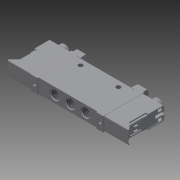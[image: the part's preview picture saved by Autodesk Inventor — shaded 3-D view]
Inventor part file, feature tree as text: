
AUTODESK INVENTOR PART (.ipt)
format: ipt  version: 2014 SP2 (Build 180246200, 246)  size: 827,904 bytes
history: native  units: mm
features: other x112, sketch x70, extrude x53, revolve x13, hole x4, thread x3
ambient origin geometry x8: Origin, YZ Plane, XZ Plane, XY Plane, X Axis, Y Axis, Z Axis, Center Point
bodies: Solid1 (feature_tree)
feature tree (255):
  extrude  "Extrusion1"  Depth=12.0mm TaperAngle=0.0deg
  extrude  "Extrusion2"  TaperAngle=360.0deg  [1 undecoded]
  extrude  "Extrusion3"  TaperAngle=360.0deg  [1 undecoded]
  sketch  "Sketch_5"  dims[d4=12.0mm d5=0.0mm d6=360.0deg]
  sketch  "Sketch_6"  dims[d7=5.4585mm d8=0.0mm d9=360.0deg]
  sketch  "Sketch_7"  dims[d10=5.4585mm d11=0.0mm d12=360.0deg d13=5.4585mm d14=0.0mm]
  revolve  "Revolution1"  Angle=360.0deg
  thread  "Thread1"  [1 undecoded]
  revolve  "Revolution2"  [1 undecoded]
  thread  "Thread2"  [1 undecoded]
  revolve  "Revolution3"  [1 undecoded]
  thread  "Thread3"  [1 undecoded]
  hole  "Hole1"  [1 undecoded]
  hole  "Hole2"  [1 undecoded]
  hole  "Hole3"  [1 undecoded]
  hole  "Hole4"  [1 undecoded]
  extrude  "Extrusion4"  Depth=5.7mm TaperAngle=0.0deg
  extrude  "Extrusion5"  Depth=4.0mm TaperAngle=0.0deg
  sketch  "Sketch_19"  dims[d57=3.1mm d58=0.0mm d59=0.1mm d60=0.0mm]
  extrude  "Extrusion6"  Depth=5.0mm TaperAngle=0.0deg
  extrude  "Extrusion7"  Depth=12.0mm TaperAngle=0.0deg
  extrude  "Extrusion8"  Depth=3.1mm TaperAngle=0.0deg
  extrude  "Extrusion9"  Depth=1.0mm TaperAngle=0.0deg
  extrude  "Extrusion10"  TaperAngle=360.0deg  [1 undecoded]
  extrude  "Extrusion11"  TaperAngle=360.0deg  [1 undecoded]
  extrude  "Extrusion12"  Depth=3.0mm TaperAngle=0.0deg
  extrude  "Extrusion13"  TaperAngle=360.0deg  [1 undecoded]
  extrude  "Extrusion14"  TaperAngle=360.0deg  [1 undecoded]
  revolve  "Revolution4"  Angle=360.0deg
  extrude  "Extrusion15"  Depth=2.15mm TaperAngle=0.0deg
  extrude  "Extrusion16"  Depth=7.8mm TaperAngle=0.0deg
  extrude  "Extrusion17"  Depth=2.1mm TaperAngle=0.0deg
  extrude  "Extrusion18"  Depth=7.8mm TaperAngle=0.0deg
  extrude  "Extrusion19"  Depth=2.8mm TaperAngle=0.0deg
  extrude  "Extrusion20"  Depth=1.5mm TaperAngle=0.0deg
  extrude  "Extrusion21"  Depth=3.0mm TaperAngle=0.0deg
  extrude  "Extrusion22"  Depth=3.0mm TaperAngle=0.0deg
  extrude  "Extrusion23"  Depth=2.0mm TaperAngle=0.0deg
  extrude  "Extrusion24"  Depth=2.0mm TaperAngle=0.0deg
  extrude  "Extrusion25"  Depth=2.0mm TaperAngle=0.0deg
  extrude  "Extrusion26"  [1 undecoded]
  extrude  "Extrusion27"  [1 undecoded]
  extrude  "Extrusion28"  [1 undecoded]
  revolve  "Revolution5"  [1 undecoded]
  revolve  "Revolution6"  [1 undecoded]
  revolve  "Revolution7"  [1 undecoded]
  sketch  "Sketch_59"
  sketch  "Sketch_56"
  extrude  "Extrusion29"  [1 undecoded]
  extrude  "Extrusion30"  [1 undecoded]
  revolve  "Revolution8"  [1 undecoded]
  revolve  "Revolution9"  [1 undecoded]
  revolve  "Revolution10"  [1 undecoded]
  revolve  "Revolution11"  [1 undecoded]
  revolve  "Revolution12"  [1 undecoded]
  revolve  "Revolution13"  [1 undecoded]
  extrude  "Extrusion31"  [1 undecoded]
  extrude  "Extrusion32"  [1 undecoded]
  extrude  "Extrusion33"  [1 undecoded]
  extrude  "Extrusion34"  [1 undecoded]
  extrude  "Extrusion35"  [1 undecoded]
  extrude  "Extrusion36"  [1 undecoded]
  extrude  "Extrusion37"  [1 undecoded]
  extrude  "Extrusion38"  [1 undecoded]
  extrude  "Extrusion39"  [1 undecoded]
  extrude  "Extrusion40"  [1 undecoded]
  extrude  "Extrusion41"  [1 undecoded]
  extrude  "Extrusion42"  [1 undecoded]
  extrude  "Extrusion43"  [1 undecoded]
  extrude  "Extrusion44"  [1 undecoded]
  extrude  "Extrusion45"  [1 undecoded]
  extrude  "Extrusion46"  [1 undecoded]
  extrude  "Extrusion47"  [1 undecoded]
  extrude  "Extrusion48"  [1 undecoded]
  extrude  "Extrusion49"  [1 undecoded]
  extrude  "Extrusion50"  [1 undecoded]
  extrude  "Extrusion51"  [1 undecoded]
  extrude  "Extrusion52"  [1 undecoded]
  extrude  "Extrusion53"  [1 undecoded]
  other  "DICHTUNG_XY"
  other  "DICHTUNG_YZ"
  other  "DICHTUNG_ZX"
  other  "DICHTUNG_X"
  other  "DICHTUNG_Y"
  other  "DICHTUNG_Z"
  other  "DICHTUNG_Center"
  other  "GEHAUSE_XY"
  other  "GEHAUSE_YZ"
  other  "GEHAUSE_ZX"
  other  "GEHAUSE_X"
  other  "GEHAUSE_Y"
  other  "GEHAUSE_Z"
  other  "GEHAUSE_Center"
  other  "HHB1_XY"
  other  "HHB1_YZ"
  other  "HHB1_ZX"
  other  "HHB1_X"
  other  "HHB1_Y"
  other  "HHB1_Z"
  other  "HHB1_Center"
  other  "HHB2_XY"
  other  "HHB2_YZ"
  other  "HHB2_ZX"
  other  "HHB2_X"
  other  "HHB2_Y"
  other  "HHB2_Z"
  other  "HHB2_Center"
  other  "NEBV1_XY"
  other  "NEBV1_YZ"
  other  "NEBV1_ZX"
  other  "NEBV1_X"
  other  "NEBV1_Y"
  other  "NEBV1_Z"
  other  "NEBV1_Center"
  other  "NEBV2_XY"
  other  "NEBV2_YZ"
  other  "NEBV2_ZX"
  other  "NEBV2_X"
  other  "NEBV2_Y"
  other  "NEBV2_Z"
  other  "NEBV2_Center"
  other  "QS_K1_XY"
  other  "QS_K1_YZ"
  other  "QS_K1_ZX"
  other  "QS_K1_X"
  other  "QS_K1_Y"
  other  "QS_K1_Z"
  other  "QS_K1_Center"
  other  "QS_K1214_XY"
  other  "QS_K1214_YZ"
  other  "QS_K1214_ZX"
  other  "QS_K1214_X"
  other  "QS_K1214_Y"
  other  "QS_K1214_Z"
  other  "QS_K1214_Center"
  other  "QS_K2_XY"
  other  "QS_K2_YZ"
  other  "QS_K2_ZX"
  other  "QS_K2_X"
  other  "QS_K2_Y"
  other  "QS_K2_Z"
  other  "QS_K2_Center"
  other  "QS_K3_XY"
  other  "QS_K3_YZ"
  other  "QS_K3_ZX"
  other  "QS_K3_X"
  other  "QS_K3_Y"
  other  "QS_K3_Z"
  other  "QS_K3_Center"
  other  "QS_K4_XY"
  other  "QS_K4_YZ"
  other  "QS_K4_ZX"
  other  "QS_K4_X"
  other  "QS_K4_Y"
  other  "QS_K4_Z"
  other  "QS_K4_Center"
  other  "QS_K5_XY"
  other  "QS_K5_YZ"
  other  "QS_K5_ZX"
  other  "QS_K5_X"
  other  "QS_K5_Y"
  other  "QS_K5_Z"
  other  "QS_K5_Center"
  other  "SCREW1_XY"
  other  "SCREW1_YZ"
  other  "SCREW1_ZX"
  other  "SCREW1_X"
  other  "SCREW1_Y"
  other  "SCREW1_Z"
  other  "SCREW1_Center"
  other  "SCREW2_XY"
  other  "SCREW2_YZ"
  other  "SCREW2_ZX"
  other  "SCREW2_X"
  other  "SCREW2_Y"
  other  "SCREW2_Z"
  other  "SCREW2_Center"
  other  "VAVE1_XY"
  other  "VAVE1_YZ"
  other  "VAVE1_ZX"
  other  "VAVE1_X"
  other  "VAVE1_Y"
  other  "VAVE1_Z"
  other  "VAVE1_Center"
  other  "VAVE2_XY"
  other  "VAVE2_YZ"
  other  "VAVE2_ZX"
  other  "VAVE2_X"
  other  "VAVE2_Y"
  other  "VAVE2_Z"
  other  "VAVE2_Center"
  sketch  "Sketch_53"  dims[d147=2.0mm d148=0.0mm d149=2.0mm d150=0.0mm]
  sketch  "Sketch_54"  dims[d151=2.0mm d152=0.0mm]
  sketch  "Sketch_55"  dims[d153=0.0mm d154=0.0mm d155=0.0mm d156=0.0mm d157=0.0mm d158=0.0mm d159=0.0mm d160=0.0mm d161=0.0mm d162=0.0mm]
  sketch  "Sketch7"  dims[d15=5.917468mm d16=6.5415mm d17=7.0mm d18=2.0mm d19=90.0deg d20=6.8mm d21=0.0mm]
  sketch  "Sketch8"  dims[d22=5.917468mm d23=6.5415mm d24=7.0mm d25=2.0mm d26=90.0deg d27=6.8mm d28=0.0mm]
  sketch  "Sketch9"  dims[d29=3.0mm d30=6.0mm d31=4.0mm d32=2.0mm d33=90.0deg d34=6.7mm d35=0.0mm]
  sketch  "Sketch10"  dims[d36=3.0mm d37=6.0mm d38=4.0mm d39=2.0mm d40=90.0deg d41=6.7mm d42=0.0mm d43=33.1mm d44=0.0mm d45=5.7mm d46=0.0mm]
  sketch  "Sketch_17"  dims[d53=12.0mm d54=0.0mm d55=12.0mm d56=0.0mm]
  sketch  "Sketch_20"  dims[d61=1.0mm d62=0.0mm d63=2.6mm d64=0.0mm]
  sketch  "Sketch_30"  dims[d97=3.0mm d98=0.0mm d99=3.0mm d100=0.0mm]
  sketch  "Sketch_22"  dims[d68=33.1mm d69=0.0mm d70=5.7mm d71=0.0mm]
  sketch  "Sketch_23"  dims[d72=64.0mm d73=0.0mm d74=4.0mm d75=0.0mm]
  sketch  "Sketch_24"  dims[d76=12.0mm d77=0.0mm d78=5.0mm d79=0.0mm]
  sketch  "Sketch_25"  dims[d80=17.2mm d81=0.0mm d82=12.0mm d83=0.0mm]
  sketch  "Sketch_26"  dims[d84=12.0mm d85=0.0mm d86=3.1mm d87=0.0mm]
  sketch  "Sketch_27"  dims[d88=0.1mm d89=0.0mm d90=1.0mm d91=0.0mm]
  sketch  "Sketch_28"  dims[d92=2.6mm d93=0.0mm d94=360.0deg]
  sketch  "Sketch_29"  dims[d95=360.0deg d96=360.0deg]
  sketch  "Sketch_21"  dims[d65=360.0deg d66=4.0mm d67=0.0mm]
  sketch  "Sketch_31"  dims[d101=360.0deg d102=360.0deg]
  sketch  "Sketch_32"  dims[d103=360.0deg d104=360.0deg]
  sketch  "Sketch_33"  dims[d105=360.0deg d106=360.0deg]
  sketch  "Sketch_119"
  sketch  "Sketch_36"  dims[d111=7.8mm d112=0.0mm d113=7.8mm d114=0.0mm]
  sketch  "Sketch_37"  dims[d115=2.1mm d116=0.0mm d117=2.1mm d118=0.0mm]
  sketch  "Sketch_38"  dims[d119=7.8mm d120=0.0mm d121=7.8mm d122=0.0mm]
  sketch  "Sketch_39"  dims[d123=7.8mm d124=0.0mm d125=2.8mm d126=0.0mm]
  sketch  "Sketch_40"  dims[d127=2.8mm d128=0.0mm d129=1.5mm d130=0.0mm]
  sketch  "Sketch_41"  dims[d131=1.5mm d132=0.0mm d133=3.0mm d134=0.0mm]
  sketch  "Sketch_42"  dims[d135=3.0mm d136=0.0mm d137=3.0mm d138=0.0mm]
  sketch  "Sketch_43"  dims[d139=3.0mm d140=0.0mm d141=2.0mm d142=0.0mm]
  sketch  "Sketch_44"  dims[d143=2.0mm d144=0.0mm d145=2.0mm d146=0.0mm]
  sketch  "Sketch_34"  dims[d107=2.15mm d108=0.0mm d109=2.15mm d110=0.0mm]
  sketch  "Sketch_4"  dims[d0=42.0mm d1=0.0mm d2=12.0mm d3=0.0mm]
  sketch  "Sketch_61"
  sketch  "Sketch_57"
  sketch  "Sketch_62"
  sketch  "Sketch_58"
  sketch  "Sketch_63"
  sketch  "Sketch_64"
  sketch  "Sketch_65"
  sketch  "Sketch_60"
  sketch  "Sketch_66"
  sketch  "Sketch_80"
  sketch  "Sketch_82"
  sketch  "Sketch_84"
  sketch  "Sketch_81"
  sketch  "Sketch_87"
  sketch  "Sketch_88"
  sketch  "Sketch_85"
  sketch  "Sketch_86"
  sketch  "Sketch_94"
  sketch  "Sketch_132"
  sketch  "Sketch_133"
  sketch  "Sketch_134"
  sketch  "Sketch_135"
  sketch  "Sketch_136"
  sketch  "Sketch_137"
  sketch  "Sketch_12"  dims[d47=5.0mm d48=0.0mm d49=12.0mm d50=0.0mm d51=17.2mm d52=0.0mm]
  sketch  "Sketch_68"
  sketch  "Sketch_101"
  sketch  "Sketch_102"
  sketch  "Sketch_103"
  sketch  "Sketch_104"
note: 52 required parameter values undecoded (feature->parameter linkage not recoverable at this tier; creation-order binding heuristic only, values carry confidence <= 0.55)